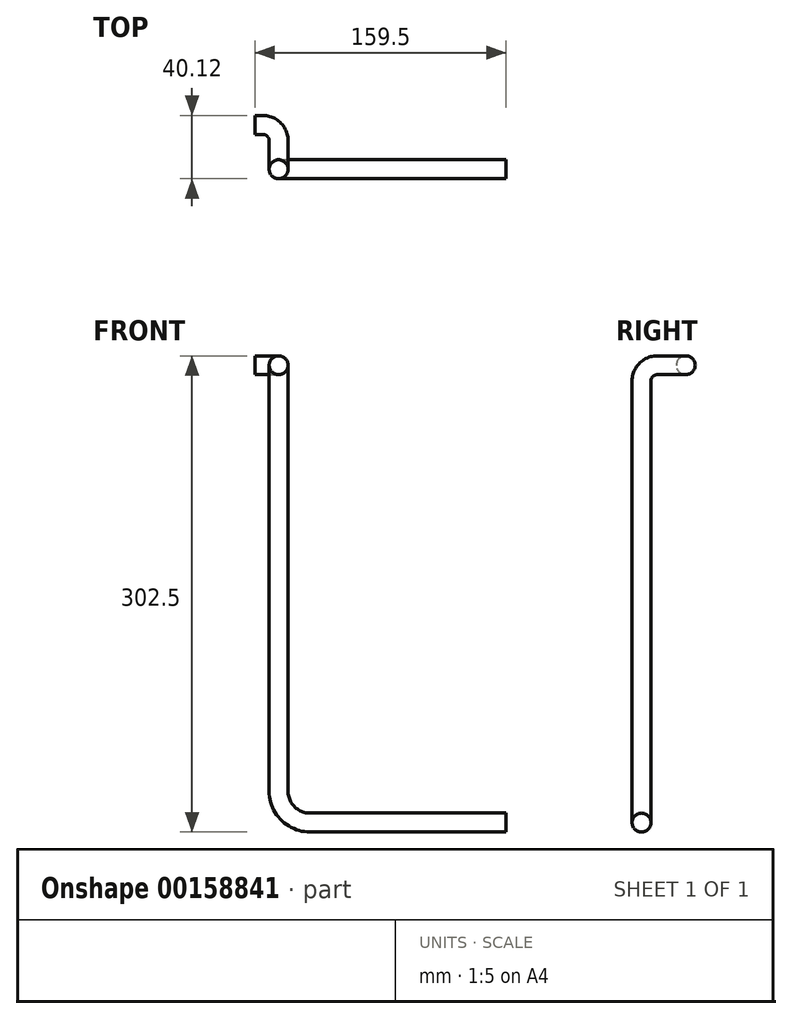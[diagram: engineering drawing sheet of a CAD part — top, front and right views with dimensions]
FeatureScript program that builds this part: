
annotation { "Feature Type Name" : "Feature", "Feature Type Description" : "" }
export const myFeature = defineFeature(function(context is Context, id is Id, definition is map)
    precondition{}
    {
        {
            var Q0;
            Q0=qCreatedBy(makeId("Top.planeOp"),FACE);
            var sketch = newSketch(context, id + "F0", { "sketchPlane" : qUnion([Q0])});
            skLineSegment(sketch, "E0", {"start": v(0, 0) * mm, "end": v(5, 0) * mm});
            skLineSegment(sketch, "E1", {"start": v(15, -10) * mm, "end": v(15, -18.12) * mm});
            skPoint(sketch, "E2.visualSharp", {"position": v(15, 0) * mm});
            skArc(sketch, "E2.filletArc", {"start": v(15, -10) * mm, "mid": v(12.07, -2.93) * mm, "end": v(5, 0) * mm});
            skSolve(sketch);
        }
        {
            var Q0;
            Q0=qCreatedBy(makeId("Front.planeOp"),FACE);
            cPlane(context, id + "F1", {"entities" : qUnion([Q0]), "cplaneType" : CPlaneType.OFFSET, "offset" : 28.12 * mm, "width" : 150 * mm, "height" : 150 * mm});
        }
        {
            var Q0;
            Q0=qCreatedBy(id+"F1.planeOp",FACE);
            var sketch = newSketch(context, id + "F2", { "sketchPlane" : qUnion([Q0])});
            skPoint(sketch, "E3.0", {"position": v(15, 0) * mm});
            skLineSegment(sketch, "E4", {"start": v(15, -20) * mm, "end": v(15, -270.5) * mm});
            skLineSegment(sketch, "E5", {"start": v(35, -290.5) * mm, "end": v(159.5, -290.5) * mm});
            skPoint(sketch, "E6.visualSharp", {"position": v(15, -290.5) * mm});
            skArc(sketch, "E6.filletArc", {"start": v(15, -270.5) * mm, "mid": v(20.86, -284.64) * mm, "end": v(35, -290.5) * mm});
            skLineSegment(sketch, "E7", {"start": v(35, 0) * mm, "end": v(139.14, 0) * mm, "construction": true});
            skArc(sketch, "E8.filletArc", {"start": v(35, 0) * mm, "mid": v(20.86, -5.86) * mm, "end": v(15, -20) * mm, "construction": true});
            skSolve(sketch);
        }
        {
            var Q0;
            Q0=qCreatedBy(makeId("Right.planeOp"),FACE);
            cPlane(context, id + "F3", {"entities" : qUnion([Q0]), "cplaneType" : CPlaneType.OFFSET, "offset" : 15 * mm, "width" : 150 * mm, "height" : 150 * mm});
        }
        {
            var Q0;
            Q0=qCreatedBy(id+"F3.planeOp",FACE);
            var sketch = newSketch(context, id + "F4", { "sketchPlane" : qUnion([Q0])});
            skPoint(sketch, "E9.0", {"position": v(-28.12, -20) * mm});
            skLineSegment(sketch, "E10", {"start": v(-28.12, -20) * mm, "end": v(-28.12, -10) * mm});
            skPoint(sketch, "E11.visualSharp", {"position": v(-28.12, 0) * mm});
            skArc(sketch, "E11.filletArc", {"start": v(-18.12, 0) * mm, "mid": v(-25.2, -2.93) * mm, "end": v(-28.12, -10) * mm});
            skSolve(sketch);
        }
        {
            var Q0;
            Q0=qCreatedBy(makeId("Right.planeOp"),FACE);
            var sketch = newSketch(context, id + "F5", { "sketchPlane" : qUnion([Q0])});
            skCircle(sketch, "E12", {"center": v(0, 0) * mm, "radius": 6 * mm});
            skSolve(sketch);
        }
        {
            var Q0;
            Q0=makeQuery(id+"F5.imprint","IMPRINT",FACE,{"disambiguationData":[TD([[makeQuery(id+"F5.imprint","IMPRINT",EDGE,{"derivedFrom":sQuery(id+"F5.wireOp",EDGE,"E12")}),1.0]])]});
            var Q1;
            Q1=sQuery(id+"F0.wireOp",EDGE,"E0");
            var Q2;
            Q2=sQuery(id+"F0.wireOp",EDGE,"E2.filletArc");
            var Q3;
            Q3=sQuery(id+"F0.wireOp",EDGE,"E1");
            var Q4;
            Q4=sQuery(id+"F4.wireOp",EDGE,"E11.filletArc");
            var Q5;
            Q5=sQuery(id+"F4.wireOp",EDGE,"E10");
            var Q6;
            Q6=sQuery(id+"F2.wireOp",EDGE,"E4");
            var Q7;
            Q7=sQuery(id+"F2.wireOp",EDGE,"E6.filletArc");
            var Q8;
            Q8=sQuery(id+"F2.wireOp",EDGE,"E5");
            sweep(context, id + "F6", {"profiles" : qUnion([Q0]), "path" : qUnion([Q1, Q2, Q3, Q4, Q5, Q6, Q7, Q8])});
        }
    });
